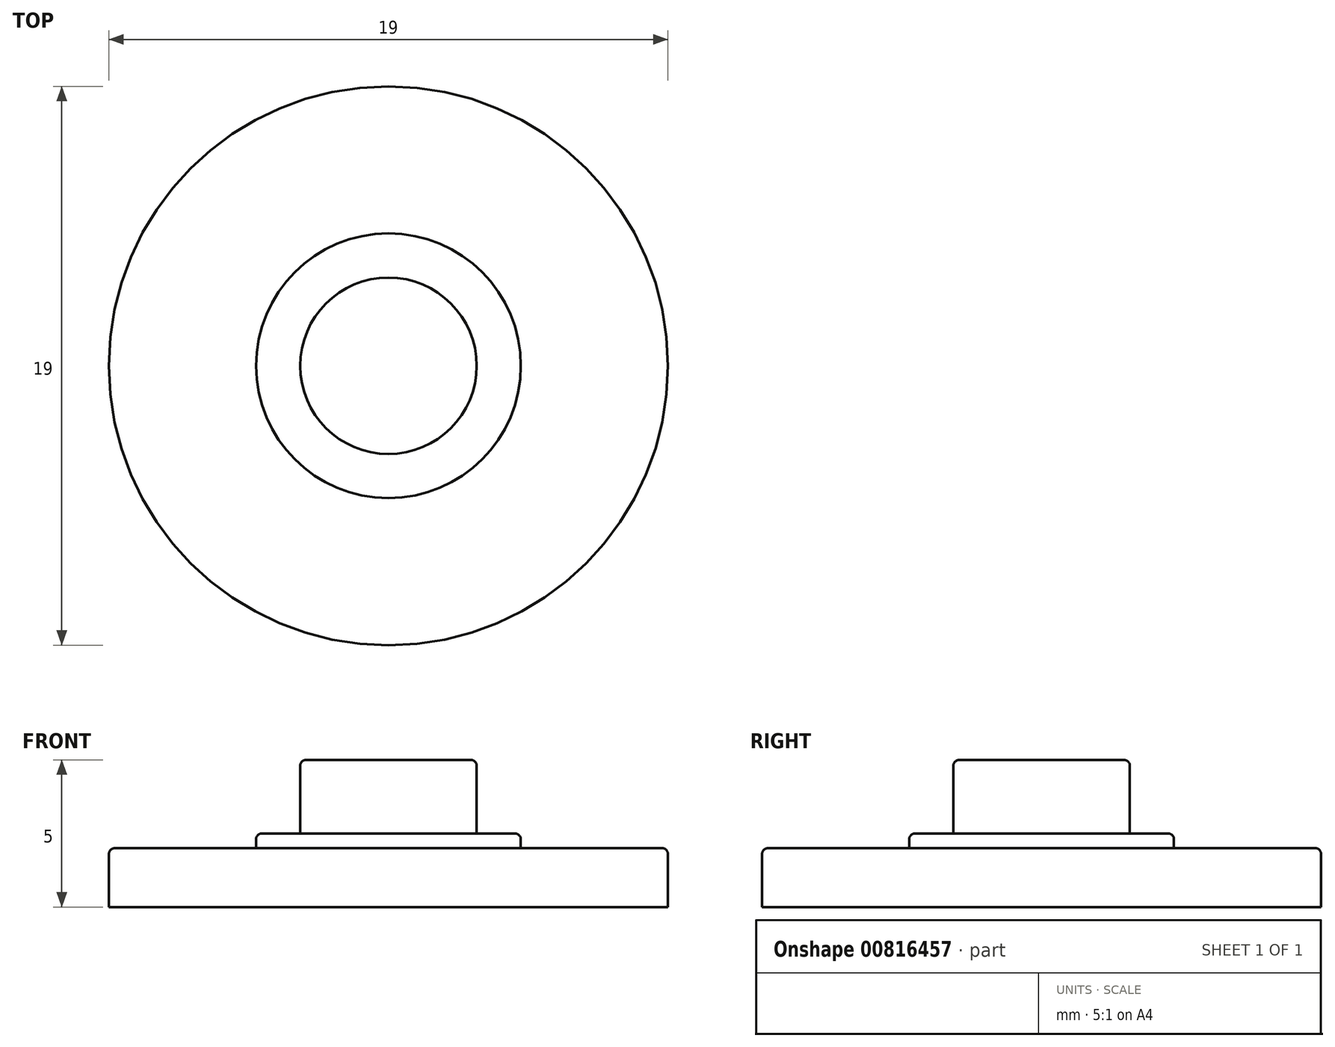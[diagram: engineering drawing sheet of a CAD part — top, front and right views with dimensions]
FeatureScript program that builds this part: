
annotation { "Feature Type Name" : "Feature", "Feature Type Description" : "" }
export const myFeature = defineFeature(function(context is Context, id is Id, definition is map)
    precondition{}
    {
        {
            var Q0;
            Q0=qCreatedBy(makeId("Top.planeOp"),FACE);
            var sketch = newSketch(context, id + "F0", { "sketchPlane" : qUnion([Q0])});
            skCircle(sketch, "E0", {"center": v(0, 0) * mm, "radius": 9.5 * mm});
            skSolve(sketch);
        }
        {
            var Q0;
            Q0 = qSketchRegion(id + "F0", true);
            extrude(context, id + "F1", {"entities" : qUnion([Q0]), "depth" : 2 * mm, "offsetDistance" : 25 * mm});
        }
        {
            var Q0;
            Q0=makeQuery(id+"F1.opExtrude","CAP_FACE",FACE,{"disambiguationData":[OSD([sQuery(id+"F0.wireOp",EDGE,"E0")])],"isStart":false});
            var sketch = newSketch(context, id + "F2", { "sketchPlane" : qUnion([Q0])});
            skCircle(sketch, "E1", {"center": v(0, 0) * mm, "radius": 4.5 * mm});
            skSolve(sketch);
        }
        {
            var Q0;
            Q0 = qSketchRegion(id + "F2", true);
            extrude(context, id + "F3", {"entities" : qUnion([Q0]), "operationType" : NewBodyOperationType.ADD, "depth" : 0.5 * mm, "offsetDistance" : 25 * mm});
        }
        {
            var Q0;
            Q0=makeQuery(id+"F3.opExtrude","CAP_FACE",FACE,{"disambiguationData":[OSD([sQuery(id+"F2.wireOp",EDGE,"E1")])],"isStart":false});
            var sketch = newSketch(context, id + "F4", { "sketchPlane" : qUnion([Q0])});
            skCircle(sketch, "E2", {"center": v(0, 0) * mm, "radius": 3 * mm});
            skSolve(sketch);
        }
        {
            var Q0;
            Q0 = qSketchRegion(id + "F4", true);
            extrude(context, id + "F5", {"entities" : qUnion([Q0]), "operationType" : NewBodyOperationType.ADD, "depth" : 2.5 * mm, "offsetDistance" : 25 * mm});
        }
        {
            var Q0;
            Q0=makeQuery(id+"F5.opExtrude","CAP_EDGE",EDGE,{"disambiguationData":[OSD([sQuery(id+"F4.wireOp",EDGE,"E2")])],"isStart":false});
            var Q1;
            Q1=makeQuery(id+"F3.opExtrude","CAP_EDGE",EDGE,{"disambiguationData":[OSD([sQuery(id+"F2.wireOp",EDGE,"E1")])],"isStart":false});
            var Q2;
            Q2=makeQuery(id+"F1.opExtrude","CAP_EDGE",EDGE,{"disambiguationData":[OSD([sQuery(id+"F0.wireOp",EDGE,"E0")])],"isStart":false});
            fillet(context, id + "F6", {"entities" : qUnion([Q0, Q1, Q2]), "radius" : 0.2 * mm, "tangentPropagation" : true, "allowEdgeOverflow" : false});
        }
    });
